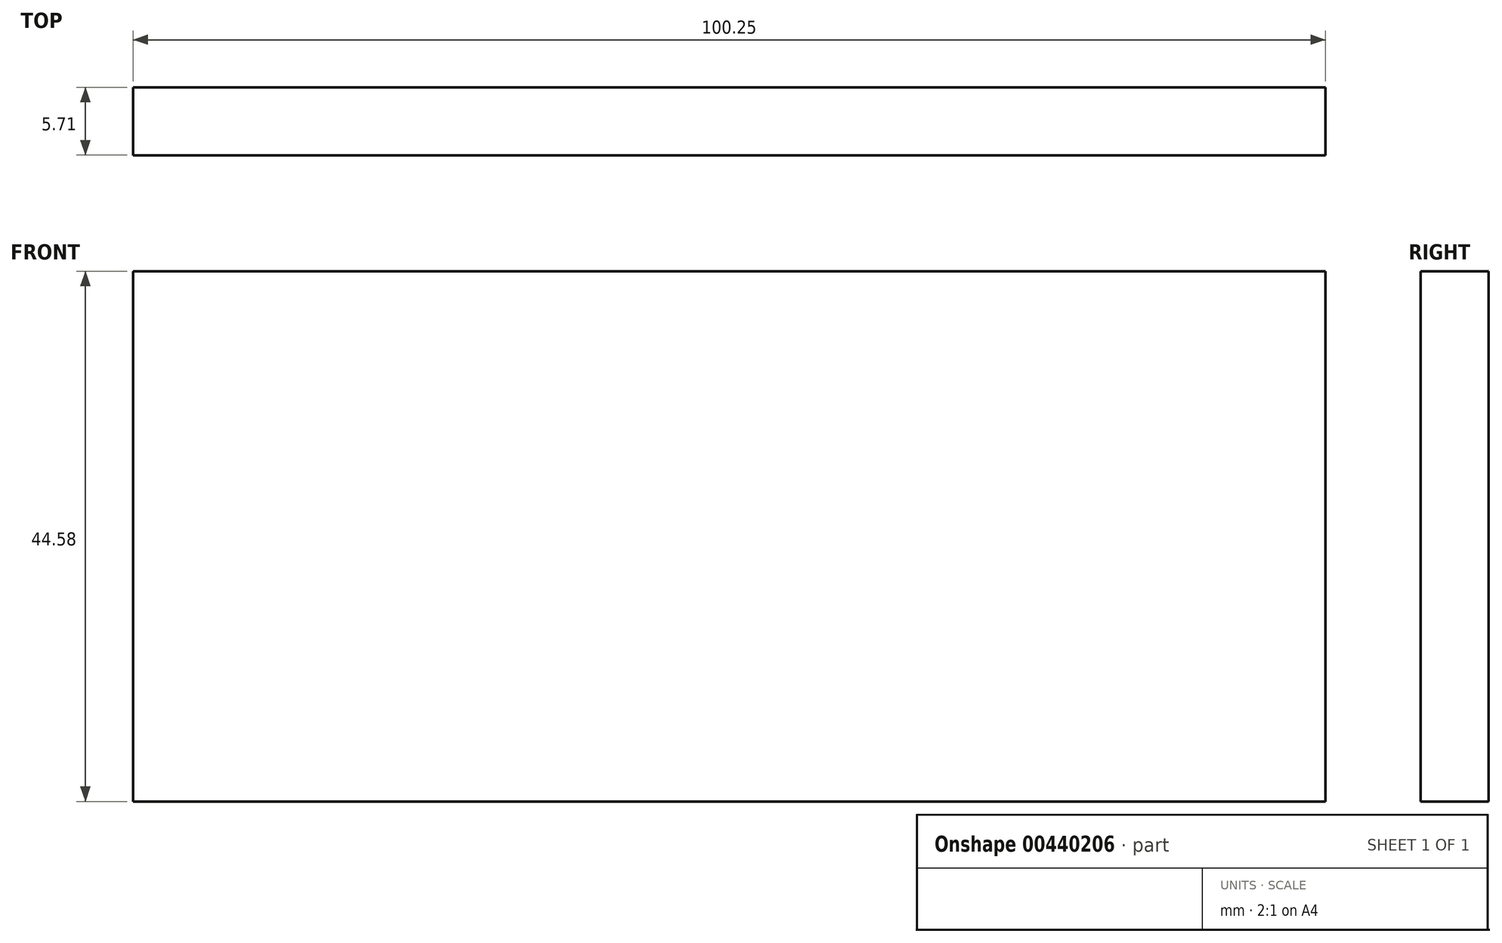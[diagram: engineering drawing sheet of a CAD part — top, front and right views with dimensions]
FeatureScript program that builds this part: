
annotation { "Feature Type Name" : "Feature", "Feature Type Description" : "" }
export const myFeature = defineFeature(function(context is Context, id is Id, definition is map)
    precondition{}
    {
        {
            var Q0;
            Q0=qCreatedBy(makeId("Front.planeOp"),FACE);
            var sketch = newSketch(context, id + "F0", { "sketchPlane" : qUnion([Q0])});
            skLineSegment(sketch, "E0", {"start": v(-34.46, 14.46) * mm, "end": v(-34.46, -30.12) * mm});
            skLineSegment(sketch, "E1", {"start": v(-34.46, -30.12) * mm, "end": v(65.8, -30.12) * mm});
            skLineSegment(sketch, "E2", {"start": v(-34.46, 14.46) * mm, "end": v(65.8, 14.46) * mm});
            skLineSegment(sketch, "E3", {"start": v(65.8, 14.46) * mm, "end": v(65.8, -30.12) * mm});
            skSolve(sketch);
        }
        {
            var Q0;
            Q0=makeQuery(id+"F0.imprint","IMPRINT",FACE,{"disambiguationData":[TD([[makeQuery(id+"F0.imprint","IMPRINT",EDGE,{"derivedFrom":sQuery(id+"F0.wireOp",EDGE,"E0")}),1.0]])]});
            extrude(context, id + "F1", {"entities" : qUnion([Q0]), "depth" : 5.7 * mm});
        }
    });
